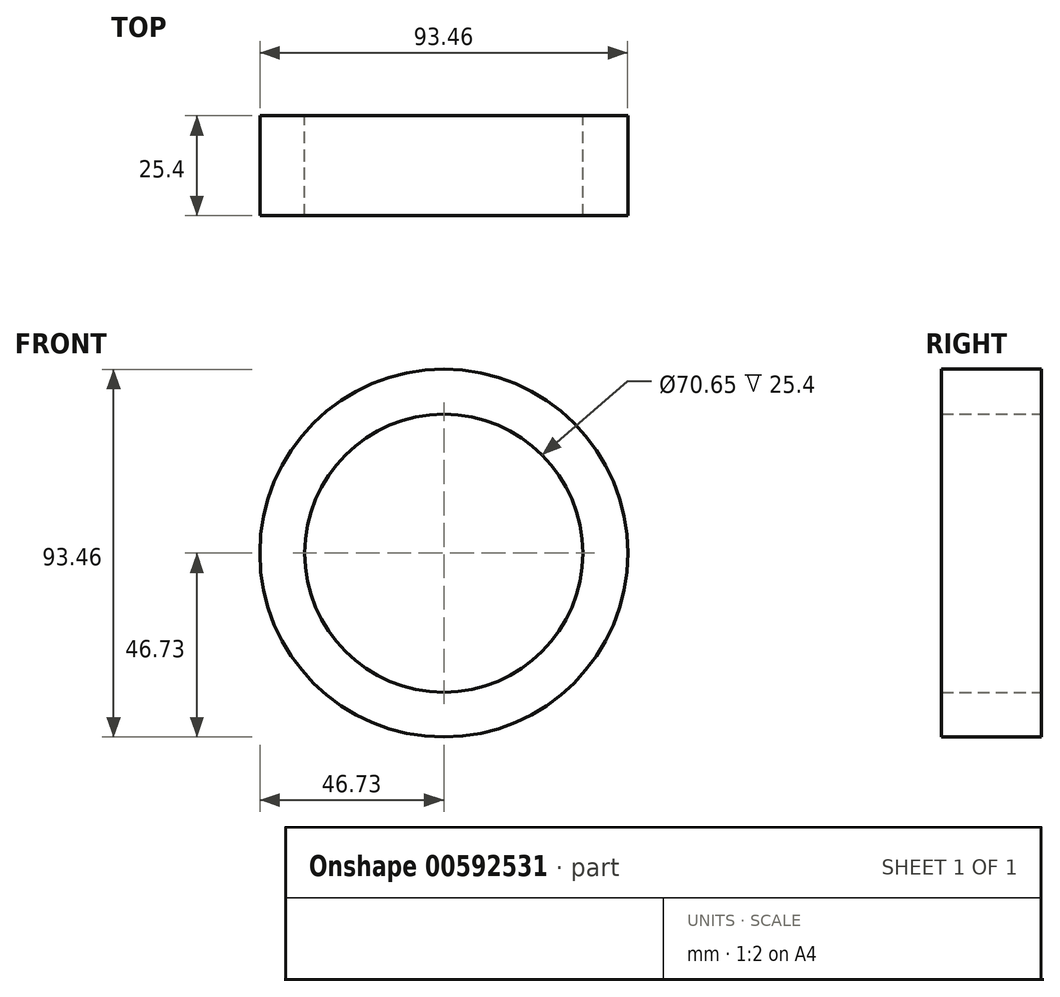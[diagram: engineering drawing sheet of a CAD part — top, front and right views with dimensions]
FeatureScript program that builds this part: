
annotation { "Feature Type Name" : "Feature", "Feature Type Description" : "" }
export const myFeature = defineFeature(function(context is Context, id is Id, definition is map)
    precondition{}
    {
        {
            var Q0;
            Q0=qCreatedBy(makeId("Front.planeOp"),FACE);
            var sketch = newSketch(context, id + "F0", { "sketchPlane" : qUnion([Q0])});
            skCircle(sketch, "E0", {"center": v(0, 0) * mm, "radius": 46.73 * mm});
            skCircle(sketch, "E1", {"center": v(0, 0) * mm, "radius": 35.33 * mm});
            skCircle(sketch, "E2", {"center": v(0, 0) * mm, "radius": 22.53 * mm});
            skLineSegment(sketch, "E3", {"start": v(-36.3, 29.44) * mm, "end": v(-26.02, 23.9) * mm});
            skLineSegment(sketch, "E4", {"start": v(-26.02, 23.9) * mm, "end": v(-26.02, 38.82) * mm});
            skSolve(sketch);
        }
        {
            var Q0;
            Q0 = qSketchRegion(id + "F0", true);
            extrude(context, id + "F1", {"entities" : qUnion([Q0]), "depth" : 25.4 * mm, "offsetDistance" : 25.4 * mm});
        }
    });
